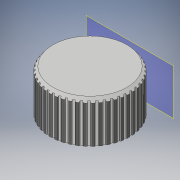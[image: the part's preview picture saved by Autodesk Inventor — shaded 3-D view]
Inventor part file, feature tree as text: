
AUTODESK INVENTOR PART (.ipt)
format: ipt  version: 2018 (Build 220112000, 112)  size: 708,096 bytes
history: native  units: mm
features: extrude x5, sketch x5, chamfer x3, fillet x2, reference x2, other x2, plane x1, pattern_circular x1, projected_geometry x1
ambient origin geometry x8: Origin, YZ Plane, XZ Plane, XY Plane, X Axis, Y Axis, Z Axis, Center Point
bodies: Volumenkörper1 (feature_tree)
feature tree (22):
  extrude  "Extrusion1"  Depth=16.0mm TaperAngle=0.0deg
  extrude  "Extrusion2"  Depth=1.0mm
  extrude  "Extrusion3"  TaperAngle=360.0deg  [1 undecoded]
  plane  "Arbeitsebene1"
  sketch  "Skizze4"  dims[d9=1.0mm d10=1.5mm d11=2.0mm d12=45.0deg]
  chamfer  "Fase1"  Distance=1.5mm Angle=45.0deg
  extrude  "Extrusion4"  Depth=10.0mm TaperAngle=360.0deg
  chamfer  "Fase3"  Distance=0.25mm Angle=45.0deg
  fillet  "Rundung1"  Radius=0.25mm
  pattern_circular  "Runde Anordnung1"  Angle=45.0deg  [1 undecoded]
  extrude  "Extrusion5"  Depth=17.25mm
  chamfer  "Fase4"  Distance=1.0mm
  fillet  "Rundung2"  Radius=10.0mm
  sketch  "Skizze1"  dims[d0=0.05mm d1=16.0mm d2=0.0mm]
  reference  "Referenz1"
  reference  "Referenz2"
  sketch  "Skizze2"  dims[d3=1.0mm d4=0.0mm d5=1.0mm]
  sketch  "Skizze3"  dims[d6=20.0mm d7=0.0mm d8=360.0deg]
  sketch  "Skizze5"  dims[d13=0.5mm d14=0.0mm d15=450.0mm d16=360.0deg d21=0.25mm d22=2.0mm d23=45.0deg d24=0.25mm d25=7.0mm d26=16.0mm d27=45.0deg d28=17.25mm d30=1.0mm d31=10.0mm d32=0.0mm]
  projected_geometry  "Projizierte Kontur1"
  parser-record x1  (decoder bookkeeping rows leaked as tree rows — omitted from the tree; the rows remain in map.json)
  other  "VolumeKnob.iam"
note: 2 required parameter values undecoded (feature->parameter linkage not recoverable at this tier; creation-order binding heuristic only, values carry confidence <= 0.55)
note: 1 file-system path scrubbed to <path> (originals preserved in map.json)
